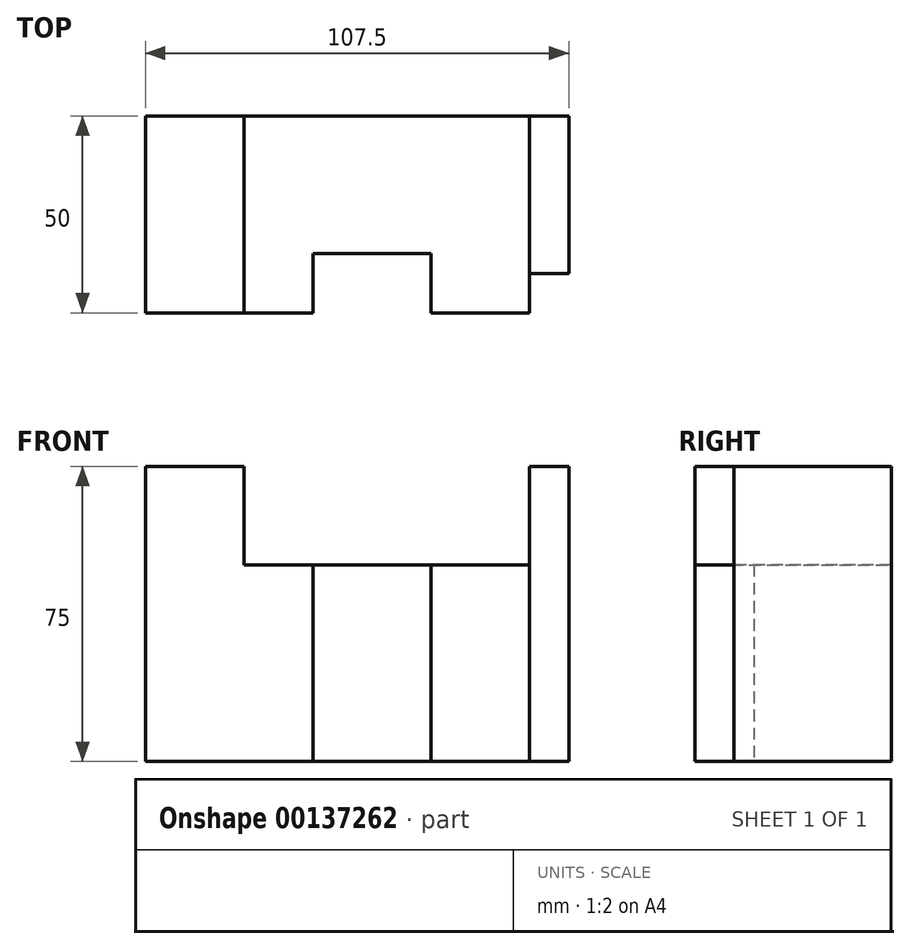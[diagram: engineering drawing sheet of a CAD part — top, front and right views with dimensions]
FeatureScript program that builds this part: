
annotation { "Feature Type Name" : "Feature", "Feature Type Description" : "" }
export const myFeature = defineFeature(function(context is Context, id is Id, definition is map)
    precondition{}
    {
        {
            var Q0;
            Q0=qCreatedBy(makeId("Front.planeOp"),FACE);
            var sketch = newSketch(context, id + "F0", { "sketchPlane" : qUnion([Q0])});
            skLineSegment(sketch, "E0", {"start": v(0, 0) * mm, "end": v(0, 75) * mm});
            skLineSegment(sketch, "E1", {"start": v(0, 75) * mm, "end": v(25, 75) * mm});
            skLineSegment(sketch, "E2", {"start": v(25, 75) * mm, "end": v(25, 0) * mm});
            skLineSegment(sketch, "E3", {"start": v(25, 0) * mm, "end": v(0, 0) * mm});
            skSolve(sketch);
        }
        {
            var Q0;
            Q0=makeQuery(id+"F0.imprint","IMPRINT",FACE,{"disambiguationData":[TD([[makeQuery(id+"F0.imprint","IMPRINT",EDGE,{"derivedFrom":sQuery(id+"F0.wireOp",EDGE,"E0")}),-1.0]])]});
            extrude(context, id + "F1", {"entities" : qUnion([Q0]), "depth" : 50 * mm});
        }
        {
            var Q0;
            Q0=makeQuery(id+"F1.opExtrude","SWEPT_FACE",FACE,{"disambiguationData":[OSD([sQuery(id+"F0.wireOp",EDGE,"E2")])]});
            var sketch = newSketch(context, id + "F2", { "sketchPlane" : qUnion([Q0])});
            skLineSegment(sketch, "E4.bottom", {"start": v(-50, 0) * mm, "end": v(0, 0) * mm});
            skLineSegment(sketch, "E4.top", {"start": v(-50, 50) * mm, "end": v(0, 50) * mm});
            skLineSegment(sketch, "E4.left", {"start": v(-50, 0) * mm, "end": v(-50, 50) * mm});
            skLineSegment(sketch, "E4.right", {"start": v(0, 0) * mm, "end": v(0, 50) * mm});
            skSolve(sketch);
        }
        {
            var Q0;
            Q0=makeQuery(id+"F2.imprint","IMPRINT",FACE,{"disambiguationData":[TD([[makeQuery(id+"F2.imprint","IMPRINT",EDGE,{"derivedFrom":sQuery(id+"F2.wireOp",EDGE,"E4.bottom")}),1.0]])]});
            extrude(context, id + "F3", {"entities" : qUnion([Q0]), "operationType" : NewBodyOperationType.ADD, "depth" : 17.5 * mm});
        }
        {
            var Q0;
            Q0=makeQuery(id+"F3.opExtrude","CAP_FACE",FACE,{"disambiguationData":[OSD([sQuery(id+"F2.wireOp",EDGE,"E4.bottom"),sQuery(id+"F2.wireOp",EDGE,"E4.top"),sQuery(id+"F2.wireOp",EDGE,"E4.left"),sQuery(id+"F2.wireOp",EDGE,"E4.right")])],"isStart":false});
            var sketch = newSketch(context, id + "F4", { "sketchPlane" : qUnion([Q0])});
            skLineSegment(sketch, "E5", {"start": v(-50, 50) * mm, "end": v(-35, 50) * mm});
            skLineSegment(sketch, "E6.bottom", {"start": v(-35, 50) * mm, "end": v(0, 50) * mm});
            skLineSegment(sketch, "E6.top", {"start": v(-35, 0) * mm, "end": v(0, 0) * mm});
            skLineSegment(sketch, "E6.left", {"start": v(-35, 50) * mm, "end": v(-35, 0) * mm});
            skLineSegment(sketch, "E6.right", {"start": v(0, 50) * mm, "end": v(0, 0) * mm});
            skLineSegment(sketch, "E7.left", {"start": v(-35, 50) * mm, "end": v(-35, 50) * mm});
            skLineSegment(sketch, "E7.right", {"start": v(0, 50) * mm, "end": v(0, 50) * mm});
            skSolve(sketch);
        }
        {
            var Q0;
            Q0=makeQuery(id+"F4.imprint","IMPRINT",FACE,{"disambiguationData":[TD([[makeQuery(id+"F4.imprint","IMPRINT",EDGE,{"derivedFrom":sQuery(id+"F4.wireOp",EDGE,"E6.top")}),1.0]])]});
            extrude(context, id + "F5", {"entities" : qUnion([Q0]), "operationType" : NewBodyOperationType.ADD, "depth" : 30 * mm});
        }
        {
            var Q0;
            Q0=makeQuery(id+"F5.opExtrude","CAP_FACE",FACE,{"disambiguationData":[OSD([sQuery(id+"F4.wireOp",EDGE,"E6.top"),sQuery(id+"F4.wireOp",EDGE,"E6.left"),sQuery(id+"F4.wireOp",EDGE,"E6.right"),sQuery(id+"F4.wireOp",EDGE,"E6.bottom")])],"isStart":false});
            var sketch = newSketch(context, id + "F6", { "sketchPlane" : qUnion([Q0])});
            skLineSegment(sketch, "E8.bottom", {"start": v(0, 50) * mm, "end": v(-50, 50) * mm});
            skLineSegment(sketch, "E8.top", {"start": v(0, 0) * mm, "end": v(-50, 0) * mm});
            skLineSegment(sketch, "E8.left", {"start": v(0, 50) * mm, "end": v(0, 0) * mm});
            skLineSegment(sketch, "E8.right", {"start": v(-50, 50) * mm, "end": v(-50, 0) * mm});
            skSolve(sketch);
        }
        {
            var Q0;
            {var subQ2=sQuery(id+"F6.wireOp",EDGE,"E8.right");Q0=makeQuery(id+"F6.imprint","IMPRINT",FACE,{"disambiguationData":[TD([[makeQuery(id+"F6.imprint","IMPRINT",EDGE,{"derivedFrom":subQ2}),1.0]])]});}
            var Q1;
            {var subQ0=sQuery(id+"F6.wireOp",EDGE,"E8.left");Q1=makeQuery(id+"F6.imprint","IMPRINT",FACE,{"disambiguationData":[TD([[makeQuery(id+"F6.imprint","IMPRINT",EDGE,{"derivedFrom":subQ0}),-1.0]])]});}
            extrude(context, id + "F7", {"entities" : qUnion([Q0, Q1]), "operationType" : NewBodyOperationType.ADD, "depth" : 25 * mm});
        }
        {
            var Q0;
            Q0=makeQuery(id+"F7.opExtrude","CAP_FACE",FACE,{"disambiguationData":[OSD([sQuery(id+"F6.wireOp",EDGE,"E8.bottom"),sQuery(id+"F6.wireOp",EDGE,"E8.top"),sQuery(id+"F6.wireOp",EDGE,"E8.left"),sQuery(id+"F6.wireOp",EDGE,"E8.right")])],"isStart":false});
            var sketch = newSketch(context, id + "F8", { "sketchPlane" : qUnion([Q0])});
            skLineSegment(sketch, "E9.bottom", {"start": v(0, 0) * mm, "end": v(-40, 0) * mm});
            skLineSegment(sketch, "E9.top", {"start": v(0, 75) * mm, "end": v(-40, 75) * mm});
            skLineSegment(sketch, "E9.left", {"start": v(0, 0) * mm, "end": v(0, 75) * mm});
            skLineSegment(sketch, "E9.right", {"start": v(-40, 0) * mm, "end": v(-40, 75) * mm});
            skSolve(sketch);
        }
        {
            var Q0;
            {var subQ0=sQuery(id+"F8.wireOp",EDGE,"E9.bottom");Q0=makeQuery(id+"F8.imprint","IMPRINT",FACE,{"disambiguationData":[TD([[makeQuery(id+"F8.imprint","IMPRINT",EDGE,{"derivedFrom":subQ0}),-1.0]])]});}
            var Q1;
            {var subQ0=sQuery(id+"F8.wireOp",EDGE,"E9.top");Q1=makeQuery(id+"F8.imprint","IMPRINT",FACE,{"disambiguationData":[TD([[makeQuery(id+"F8.imprint","IMPRINT",EDGE,{"derivedFrom":subQ0}),1.0]])]});}
            extrude(context, id + "F9", {"entities" : qUnion([Q0, Q1]), "operationType" : NewBodyOperationType.ADD, "depth" : 10 * mm});
        }
    });
